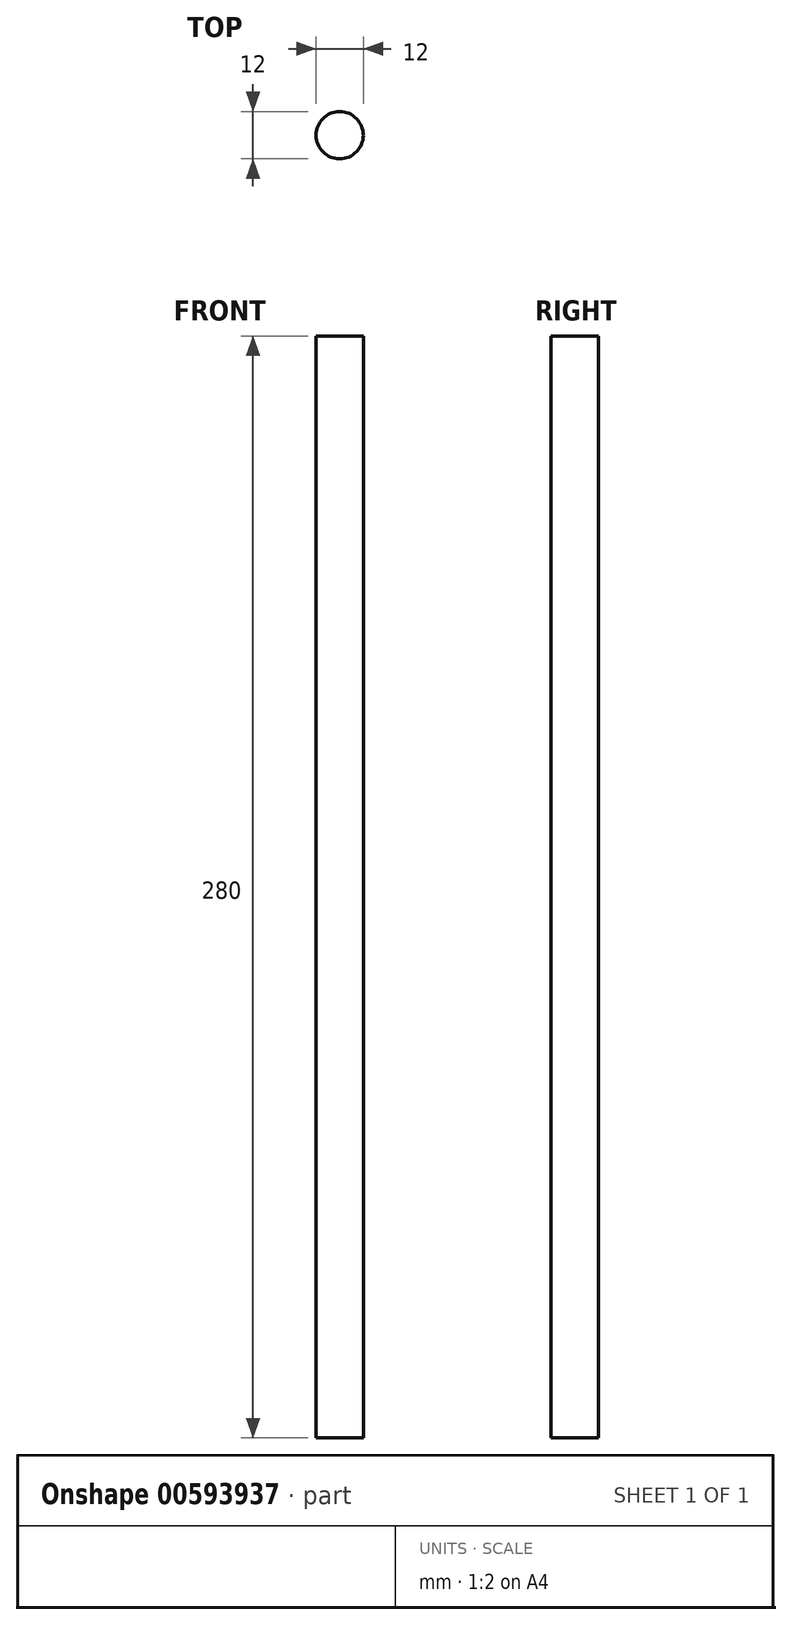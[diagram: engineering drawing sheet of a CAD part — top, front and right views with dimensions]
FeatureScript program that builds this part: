
annotation { "Feature Type Name" : "Feature", "Feature Type Description" : "" }
export const myFeature = defineFeature(function(context is Context, id is Id, definition is map)
    precondition{}
    {
        {
            var Q0;
            Q0=qCreatedBy(makeId("Top.planeOp"),FACE);
            var sketch = newSketch(context, id + "F0", { "sketchPlane" : qUnion([Q0])});
            skCircle(sketch, "E0", {"center": v(-24.82, 0) * mm, "radius": 6 * mm});
            skCircle(sketch, "E1", {"center": v(38.18, 0) * mm, "radius": 6 * mm});
            skSolve(sketch);
        }
        {
            var Q0;
            Q0=makeQuery(id+"F0.imprint","IMPRINT",FACE,{"disambiguationData":[TD([[makeQuery(id+"F0.imprint","IMPRINT",EDGE,{"derivedFrom":sQuery(id+"F0.wireOp",EDGE,"E1")}),1.0]])]});
            extrude(context, id + "F1", {"entities" : qUnion([Q0]), "depth" : 280 * mm, "offsetDistance" : 25 * mm});
        }
    });
